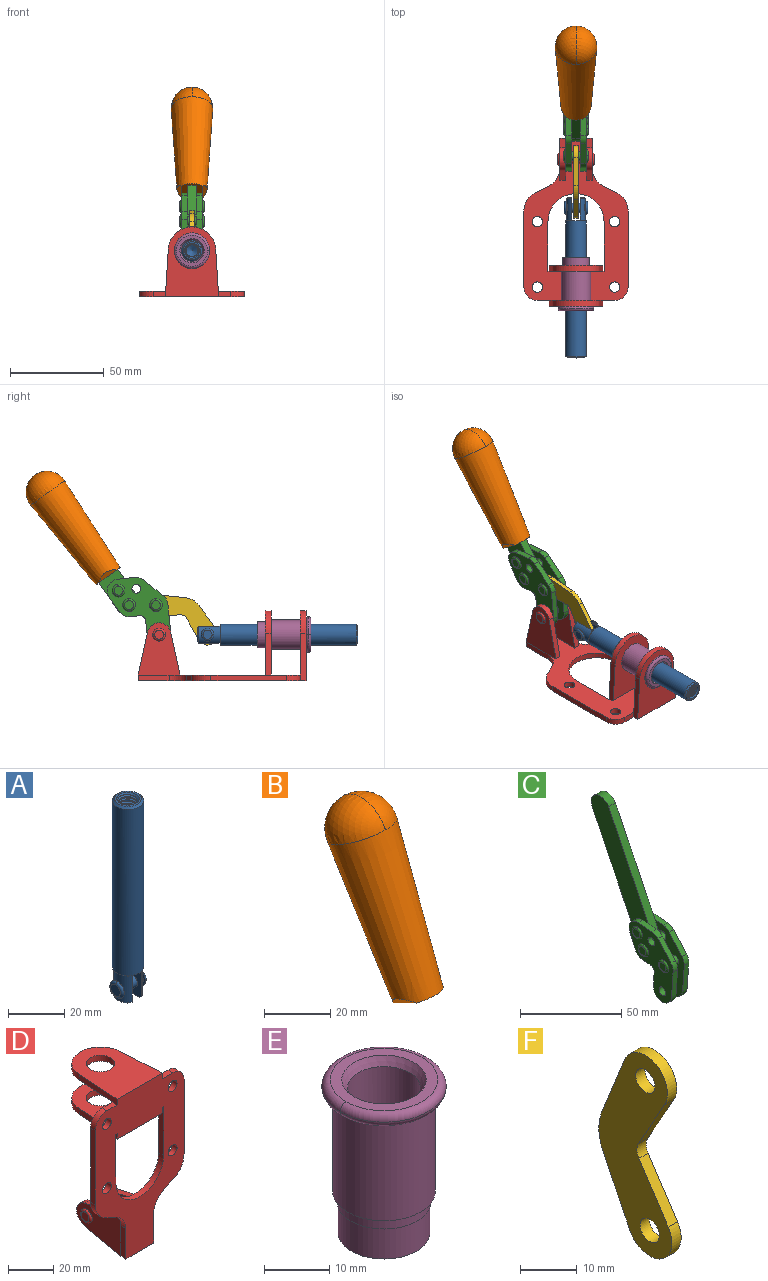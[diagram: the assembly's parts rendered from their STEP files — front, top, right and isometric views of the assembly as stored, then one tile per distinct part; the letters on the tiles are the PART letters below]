
ASSEMBLY  parts=6 mates=6
PART A: 48 faces, bbox 12.6x11.1x86.1 mm
  f0: torus R=2.41mm, axis (-1,0,0), area 15mm2, adj f30,f32,f34
  f1: torus R=2.41mm, axis (-1,0,0), area 15mm2, adj f29,f31,f33
  f2: cylinder r=5.54mm len=72.39mm, axis (0,0,1), area 2518.5mm2, adj f3,f4,f42,f43
  f3: cone r=5.54mm half-angle=45deg, axis (0,0,1), area 7.6mm2, adj f2,f5,f41
  f4: cone r=5.54mm half-angle=45deg, axis (0,0,-1), area 34.9mm2, adj f2,f39
  f5: cylinder r=5.08mm len=11.48mm, axis (0,0,1), area 108.3mm2, adj f3,f7,f8,f41
  f6: cylinder r=2.41mm len=4.83mm, axis (-1,0,0), area 71.2mm2, adj f40,f41
  f7: cylinder r=2.41mm len=4.83mm, axis (-1,0,0), area 7.6mm2, adj f5,f34
  f8: cone r=5.08mm half-angle=45deg, axis (0,0,1), area 10.6mm2, adj f5,f37,f41
  f9: cone r=3.98mm half-angle=45deg, axis (0,0,1), area 17.6mm2, adj f27,f39,f45,f46,f47
  f10: cylinder r=2.41mm len=4.83mm, axis (-1,0,0), area 7.6mm2, adj f33,f38
  f11: cylinder r=3.2mm len=6.4mm, axis (0,0,1), area 78.4mm2, adj f12,f28,f44,f45,f47
  f12: cylinder r=3.2mm len=6.4mm, axis (0,0,1), area 10.5mm2, adj f11,f13,f45,f47
  f13: cylinder r=3.2mm len=6.4mm, axis (0,0,1), area 10.5mm2, adj f12,f14,f45,f47
  f14: cylinder r=3.2mm len=6.4mm, axis (0,0,1), area 10.5mm2, adj f13,f15,f45,f47
  f15: cylinder r=3.2mm len=6.4mm, axis (0,0,1), area 10.5mm2, adj f14,f16,f45,f47
  f16: cylinder r=3.2mm len=6.4mm, axis (0,0,1), area 10.5mm2, adj f15,f17,f45,f47
  f17: cylinder r=3.2mm len=6.4mm, axis (0,0,1), area 10.5mm2, adj f16,f18,f45,f47
  f18: cylinder r=3.2mm len=6.4mm, axis (0,0,1), area 10.5mm2, adj f17,f19,f45,f47
  f19: cylinder r=3.2mm len=6.4mm, axis (0,0,1), area 10.5mm2, adj f18,f20,f45,f47
  f20: cylinder r=3.2mm len=6.4mm, axis (0,0,1), area 10.5mm2, adj f19,f21,f45,f47
  f21: cylinder r=3.2mm len=6.4mm, axis (0,0,1), area 10.5mm2, adj f20,f22,f45,f47
  f22: cylinder r=3.2mm len=6.4mm, axis (0,0,1), area 10.5mm2, adj f21,f23,f45,f47
  f23: cylinder r=3.2mm len=6.4mm, axis (0,0,1), area 10.5mm2, adj f22,f24,f45,f47
  f24: cylinder r=3.2mm len=6.4mm, axis (0,0,1), area 10.5mm2, adj f23,f25,f45,f47
  f25: cylinder r=3.2mm len=6.4mm, axis (0,0,1), area 10.5mm2, adj f24,f26,f45,f47
  f26: cylinder r=3.2mm len=6.4mm, axis (0,0,1), area 10.5mm2, adj f25,f27,f45,f47
  f27: cylinder r=3.2mm len=6.4mm, axis (0,0,1), area 7.4mm2, adj f9,f26,f45,f47
  f28: cone r=3.2mm half-angle=60deg, axis (0,0,1), area 37.2mm2, adj f11
  f29: plane 4.83x4.83mm, normal (-1,0,0), area 18.3mm2, adj f1,f31
  f30: plane 4.83x4.83mm, normal (1,0,0), area 18.3mm2, adj f0,f32
  f31: torus R=2.41mm, axis (-1,0,0), area 15mm2, adj f1,f29,f33
  f32: torus R=2.41mm, axis (-1,0,0), area 15mm2, adj f0,f30,f34
  f33: plane 6.83x6.83mm, normal (1,0,0), area 18.3mm2, adj f1,f10,f31
  f34: plane 6.83x6.83mm, normal (-1,0,0), area 18.3mm2, adj f0,f7,f32
  f35: cone r=5.08mm half-angle=45deg, axis (0,0,1), area 10.6mm2, adj f36,f38,f40
  f36: plane 7.25x1.97mm, normal (0,0,-1), area 10mm2, adj f35,f40
  f37: plane 7.25x1.97mm, normal (0,0,-1), area 10mm2, adj f8,f41
  f38: cylinder r=5.08mm len=11.48mm, axis (0,0,1), area 108.3mm2, adj f10,f35,f40,f42
  f39: plane 9.55x9.55mm, normal (0,0,1), area 22mm2, adj f4,f9
  f40: plane 12.76x10.09mm, normal (1,0,0), area 95.7mm2, adj f6,f35,f36,f38,f42,f43
  f41: plane 12.76x10.09mm, normal (-1,0,0), area 95.7mm2, adj f3,f5,f6,f8,f37,f43
  f42: cone r=5.54mm half-angle=45deg, axis (0,0,1), area 7.6mm2, adj f2,f38,f40
  f43: plane 11.07x4.7mm, normal (0,0,-1), area 50.4mm2, adj f2,f40,f41
  f44: plane 0.89x0.62mm, normal (-1,0,0), area 0.3mm2, adj f11,f45,f46,f47
  f45: bspline ~24.8x7.63mm, area 266.6mm2, adj f9,f11,f12,f13,f14,f15,f16,f17
  f46: bspline ~24.87x7.63mm, area 73.6mm2, adj f9,f44,f45,f47
  f47: bspline ~24.98x7.63mm, area 272.5mm2, adj f9,f11,f12,f13,f14,f15,f16,f17
PART B: 11 faces, bbox 22.3x42.6x64.5 mm
  f0: sphere r=11.13mm, area 411.4mm2, adj f1,f8
  f1: cone r=11.11mm half-angle=3.3deg, axis (0,0.44,0.9), area 3251.8mm2, adj f0,f7,f8,f9,f10
  f2: cylinder r=6.16mm len=11.7mm, axis (1,0,0), area 89.5mm2, adj f3,f4,f5,f6
  f3: plane 60.23x36.75mm, normal (-1,0,0), area 763.6mm2, adj f2,f4,f6,f10
  f4: plane 51.37x25.05mm, normal (0,0.9,-0.44), area 264.2mm2, adj f2,f3,f5,f10
  f5: plane 60.23x36.75mm, normal (1,0,0), area 763.6mm2, adj f2,f4,f6,f10
  f6: plane 51.37x25.05mm, normal (0,-0.9,0.44), area 264.2mm2, adj f2,f3,f5,f10
  f7: plane 9.95x5.95mm, normal (0.71,-0.31,-0.64), area 25.8mm2, adj f1,f10
  f8: sphere r=11.13mm, area 411.4mm2, adj f0,f1
  f9: plane 9.95x5.95mm, normal (-0.71,-0.31,-0.64), area 25.8mm2, adj f1,f10
  f10: plane 14.27x11.38mm, normal (0,-0.44,-0.9), area 106.7mm2, adj f1,f3,f4,f5,f6,f7,f9
PART C: 59 faces, bbox 12.9x60.2x99.6 mm
  f0: torus R=2.39mm, axis (-1,0,0), area 14.9mm2, adj f20,f43,f51
  f1: torus R=2.39mm, axis (-1,0,0), area 14.9mm2, adj f19,f42,f51
  f2: torus R=2.39mm, axis (-1,0,0), area 14.9mm2, adj f18,f35,f51
  f3: torus R=2.39mm, axis (-1,0,0), area 14.9mm2, adj f14,f17,f23
  f4: torus R=2.39mm, axis (-1,0,0), area 14.9mm2, adj f13,f16,f23
  f5: torus R=2.39mm, axis (-1,0,0), area 14.9mm2, adj f12,f15,f23
  f6: cylinder r=2.39mm len=4.78mm, axis (1,0,0), area 46.5mm2, adj f48,f50,f51
  f7: cylinder r=2.39mm len=4.78mm, axis (1,0,0), area 46.5mm2, adj f50,f51
  f8: cylinder r=6.35mm len=12.68mm, axis (1,0,0), area 61.8mm2, adj f38,f39,f50,f51
  f9: cylinder r=2.39mm len=4.78mm, axis (-1,0,0), area 70.5mm2, adj f46,f50
  f10: cylinder r=2.39mm len=4.78mm, axis (-1,0,0), area 46.5mm2, adj f23,f45,f46
  f11: cylinder r=2.39mm len=4.78mm, axis (-1,0,0), area 46.5mm2, adj f23,f46
  f12: plane 4.78x4.78mm, normal (1,0,0), area 17.9mm2, adj f5,f15
  f13: plane 4.78x4.78mm, normal (1,0,0), area 17.9mm2, adj f4,f16
  f14: plane 4.78x4.78mm, normal (1,0,0), area 17.9mm2, adj f3,f17
  f15: torus R=2.39mm, axis (-1,0,0), area 14.9mm2, adj f5,f12,f23
  f16: torus R=2.39mm, axis (-1,0,0), area 14.9mm2, adj f4,f13,f23
  f17: torus R=2.39mm, axis (-1,0,0), area 14.9mm2, adj f3,f14,f23
  f18: plane 4.78x4.78mm, normal (-1,0,0), area 17.9mm2, adj f2,f35
  f19: plane 4.78x4.78mm, normal (-1,0,0), area 17.9mm2, adj f1,f42
  f20: plane 4.78x4.78mm, normal (-1,0,0), area 17.9mm2, adj f0,f43
  f21: plane 2.26x0.2mm, normal (1,0,0), area 0.2mm2, adj f31,f44
  f22: plane 2.26x0.2mm, normal (-1,0,0), area 0.2mm2, adj f41,f44
  f23: plane 39.37x30.77mm, normal (1,0,0), area 565.5mm2, adj f3,f4,f5,f10,f11,f15,f16,f17
  f24: cylinder r=6.1mm len=4.15mm, axis (-1,0,0), area 14.7mm2, adj f23,f25,f32,f46
  f25: plane 10.25x9.01mm, normal (0,-0.75,0.66), area 42.3mm2, adj f23,f24,f26,f46
  f26: cylinder r=6.35mm len=4.64mm, axis (-1,0,0), area 15.6mm2, adj f23,f25,f27,f46
  f27: plane 15.84x3.1mm, normal (0,-1,-0.07), area 49.2mm2, adj f23,f26,f28,f46
  f28: cylinder r=6.35mm len=12.68mm, axis (-1,0,0), area 61.8mm2, adj f23,f27,f29,f46
  f29: plane 8.11x3.1mm, normal (0,1,0.07), area 25.2mm2, adj f23,f28,f30,f46
  f30: cylinder r=3.05mm len=3.25mm, axis (-1,0,0), area 14.8mm2, adj f23,f29,f31,f46
  f31: plane 5.99x3.1mm, normal (0,0.07,-1), area 18.6mm2, adj f21,f23,f30,f44,f46
  f32: plane 9.5x3.1mm, normal (0,-0.07,1), area 29.5mm2, adj f23,f24,f33,f46,f47
  f33: cylinder r=6.1mm len=8.63mm, axis (-1,0,0), area 39.1mm2, adj f23,f32,f34,f47
  f34: plane 8.65x3.96mm, normal (0,0.91,-0.42), area 29.5mm2, adj f23,f33,f44,f47
  f35: torus R=2.39mm, axis (-1,0,0), area 14.9mm2, adj f2,f18,f51
  f36: plane 10.25x9.01mm, normal (0,-0.75,0.66), area 42.3mm2, adj f37,f49,f50,f51
  f37: cylinder r=6.35mm len=4.64mm, axis (1,0,0), area 15.6mm2, adj f36,f38,f50,f51
  f38: plane 15.84x3.1mm, normal (0,-1,-0.07), area 49.2mm2, adj f8,f37,f50,f51
  f39: plane 8.11x3.1mm, normal (0,1,0.07), area 25.2mm2, adj f8,f40,f50,f51
  f40: cylinder r=3.05mm len=3.25mm, axis (1,0,0), area 14.8mm2, adj f39,f41,f50,f51
  f41: plane 5.99x3.1mm, normal (0,0.07,-1), area 18.6mm2, adj f22,f40,f44,f50,f51
  f42: torus R=2.39mm, axis (-1,0,0), area 14.9mm2, adj f1,f19,f51
  f43: torus R=2.39mm, axis (-1,0,0), area 14.9mm2, adj f0,f20,f51
  f44: cylinder r=6.35mm len=12.12mm, axis (-1,0,0), area 128.9mm2, adj f21,f22,f23,f31,f34,f41,f46,f47
  f45: plane 2.65x1.35mm, normal (1,0,0), area 1mm2, adj f10,f55
  f46: plane 39.08x20.42mm, normal (-1,0,0), area 412.5mm2, adj f9,f10,f11,f24,f25,f26,f27,f28
  f47: plane 77.62x39.82mm, normal (1,0,0), area 850mm2, adj f32,f33,f34,f44,f53,f54,f55
  f48: plane 2.65x1.35mm, normal (-1,0,0), area 1mm2, adj f6,f55
  f49: cylinder r=6.1mm len=4.15mm, axis (1,0,0), area 14.7mm2, adj f36,f50,f51,f56
  f50: plane 39.08x20.42mm, normal (1,0,0), area 412.5mm2, adj f6,f7,f8,f9,f36,f37,f38,f39
  f51: plane 39.37x30.77mm, normal (-1,0,0), area 565.5mm2, adj f0,f1,f2,f6,f7,f8,f35,f36
  f52: plane 8.65x3.96mm, normal (0,0.91,-0.42), area 29.5mm2, adj f44,f51,f57,f58
  f53: plane 68.49x33.4mm, normal (0,0.9,-0.44), area 358.1mm2, adj f44,f47,f54,f58
  f54: cylinder r=6.35mm len=12.06mm, axis (1,0,0), area 93.7mm2, adj f47,f53,f55,f58
  f55: plane 68.49x33.4mm, normal (0,-0.9,0.44), area 358.1mm2, adj f44,f45,f46,f47,f48,f50,f54,f58
  f56: plane 9.5x3.1mm, normal (0,-0.07,1), area 29.5mm2, adj f49,f50,f51,f57,f58
  f57: cylinder r=6.1mm len=8.63mm, axis (1,0,0), area 39.1mm2, adj f51,f52,f56,f58
  f58: plane 77.62x39.82mm, normal (-1,0,0), area 850mm2, adj f44,f52,f53,f54,f55,f56,f57
PART D: 55 faces, bbox 55.7x37.4x89.8 mm
  f0: torus R=2.41mm, axis (-1,0,0), area 15mm2, adj f11,f15,f25
  f1: torus R=2.41mm, axis (-1,0,0), area 15mm2, adj f10,f12,f22
  f2: cylinder r=2.78mm len=5.56mm, axis (0,-1,0), area 54.2mm2, adj f30,f54
  f3: cylinder r=14.99mm len=29.97mm, axis (0,-1,0), area 145.9mm2, adj f30,f49,f53,f54
  f4: cylinder r=2.78mm len=5.56mm, axis (0,-1,0), area 54.2mm2, adj f30,f54
  f5: cylinder r=2.78mm len=5.56mm, axis (0,-1,0), area 54.2mm2, adj f30,f54
  f6: cylinder r=2.78mm len=5.56mm, axis (0,-1,0), area 54.2mm2, adj f30,f54
  f7: cylinder r=6.35mm len=12.7mm, axis (0,0,1), area 123.6mm2, adj f27,f51
  f8: cylinder r=6.35mm len=12.7mm, axis (0,0,-1), area 124.7mm2, adj f21,f35
  f9: cylinder r=2.41mm len=11.18mm, axis (-1,0,0), area 169.4mm2, adj f16,f19
  f10: plane 4.83x4.83mm, normal (1,0,0), area 18.3mm2, adj f1,f12
  f11: plane 4.83x4.83mm, normal (-1,0,0), area 18.3mm2, adj f0,f15
  f12: torus R=2.41mm, axis (-1,0,0), area 15mm2, adj f1,f10,f22
  f13: cylinder r=6.35mm len=12.41mm, axis (1,0,0), area 53.4mm2, adj f18,f19,f22,f23
  f14: cylinder r=6.35mm len=12.41mm, axis (-1,0,0), area 53.4mm2, adj f16,f17,f24,f25
  f15: torus R=2.41mm, axis (-1,0,0), area 15mm2, adj f0,f11,f25
  f16: plane 27.86x22.35mm, normal (1,0,0), area 425.4mm2, adj f9,f14,f17,f24,f30
  f17: plane 22.86x4.97mm, normal (0,0.21,0.98), area 72.5mm2, adj f14,f16,f25,f30
  f18: plane 22.86x4.97mm, normal (0,0.21,0.98), area 72.5mm2, adj f13,f19,f22,f30
  f19: plane 27.86x22.35mm, normal (-1,0,0), area 425.4mm2, adj f9,f13,f18,f23,f30
  f20: cylinder r=12.7mm len=25.35mm, axis (0,0,-1), area 119.8mm2, adj f21,f34,f35,f36
  f21: plane 34.21x28.07mm, normal (0,0,-1), area 702.4mm2, adj f8,f20,f30,f34,f36
  f22: plane 27.96x22.45mm, normal (1,0,0), area 407.2mm2, adj f1,f12,f13,f18,f23,f30,f42,f43
  f23: plane 22.86x4.97mm, normal (0,0.21,-0.98), area 72.5mm2, adj f13,f19,f22,f44
  f24: plane 22.86x4.97mm, normal (0,0.21,-0.98), area 72.5mm2, adj f14,f16,f25,f44
  f25: plane 27.86x22.35mm, normal (-1,0,0), area 407.1mm2, adj f0,f14,f15,f17,f24,f30,f45,f46
  f26: plane 3.1x0.95mm, normal (0,0,-1), area 2.7mm2, adj f30,f49,f50,f54
  f27: plane 34.21x28.07mm, normal (0,0,1), area 702.4mm2, adj f7,f28,f30,f50,f52
  f28: cylinder r=12.7mm len=25.35mm, axis (0,0,1), area 118.8mm2, adj f27,f50,f51,f52
  f29: plane 3.1x0.95mm, normal (0,0,-1), area 2.7mm2, adj f30,f52,f53,f54
  f30: plane 86.54x55.63mm, normal (0,1,0), area 2362.9mm2, adj f2,f3,f4,f5,f6,f16,f17,f18
  f31: plane 40.56x3.1mm, normal (-1,0,0), area 125.7mm2, adj f30,f32,f48,f54
  f32: cylinder r=7.11mm len=7.11mm, axis (0,-1,0), area 34.6mm2, adj f30,f31,f33,f54
  f33: plane 6.67x3.1mm, normal (0,0,1), area 20.4mm2, adj f30,f32,f34,f54
  f34: plane 25.39x3.13mm, normal (-1,0.06,0), area 79.5mm2, adj f20,f21,f33,f35,f54
  f35: plane 37.31x28.45mm, normal (0,0,1), area 789.9mm2, adj f8,f20,f34,f36,f54
  f36: plane 25.39x3.13mm, normal (1,0.06,0), area 79.5mm2, adj f20,f21,f35,f37,f54
  f37: plane 6.67x3.1mm, normal (0,0,1), area 20.4mm2, adj f30,f36,f38,f54
  f38: cylinder r=7.11mm len=7.11mm, axis (0,-1,0), area 34.6mm2, adj f30,f37,f39,f54
  f39: plane 40.56x3.1mm, normal (1,0,0), area 125.7mm2, adj f30,f38,f40,f54
  f40: cylinder r=11.18mm len=10.16mm, axis (0,-1,0), area 39.5mm2, adj f30,f39,f41,f54
  f41: plane 6.09x3.1mm, normal (0.42,0,-0.91), area 20.8mm2, adj f30,f40,f42,f54
  f42: cylinder r=11.18mm len=9.41mm, axis (0,-1,0), area 37.2mm2, adj f22,f30,f41,f43,f54
  f43: plane 16.5x3.1mm, normal (1,0,0), area 51.1mm2, adj f22,f42,f44,f54
  f44: plane 17.37x3.1mm, normal (0,0,-1), area 53.8mm2, adj f23,f24,f30,f43,f45,f54
  f45: plane 16.5x3.1mm, normal (-1,0,0), area 51.1mm2, adj f25,f44,f46,f54
  f46: cylinder r=11.18mm len=9.41mm, axis (0,-1,0), area 37.2mm2, adj f25,f30,f45,f47,f54
  f47: plane 6.09x3.1mm, normal (-0.42,0,-0.91), area 20.8mm2, adj f30,f46,f48,f54
  f48: cylinder r=11.18mm len=10.16mm, axis (0,-1,0), area 39.5mm2, adj f30,f31,f47,f54
  f49: plane 26.54x3.1mm, normal (-1,0,0), area 82.3mm2, adj f3,f26,f30,f54
  f50: plane 25.39x3.1mm, normal (1,0.06,0), area 78.8mm2, adj f26,f27,f28,f51,f54
  f51: plane 37.31x28.45mm, normal (0,0,-1), area 789.9mm2, adj f7,f28,f50,f52,f54
  f52: plane 25.39x3.1mm, normal (-1,0.06,0), area 78.8mm2, adj f27,f28,f29,f51,f54
  f53: plane 26.54x3.1mm, normal (1,0,0), area 82.3mm2, adj f3,f29,f30,f54
  f54: plane 89.66x55.63mm, normal (0,-1,0), area 2678.5mm2, adj f2,f3,f4,f5,f6,f26,f29,f31
PART E: 15 faces, bbox 20.6x20.6x28.7 mm
  f0: torus R=8.26mm, axis (0,0,1), area 56.8mm2, adj f1,f10,f12
  f1: torus R=8.26mm, axis (0,0,1), area 56.8mm2, adj f0,f6,f13
  f2: cylinder r=5.59mm len=25.91mm, axis (0,0,1), area 909.6mm2, adj f3,f4
  f3: cone r=6.86mm half-angle=45deg, axis (0,0,-1), area 70.2mm2, adj f2,f14
  f4: cone r=6.47mm half-angle=30deg, axis (0,0,1), area 66.7mm2, adj f2,f13
  f5: cylinder r=7.04mm len=14.07mm, axis (0,0,1), area 252.6mm2, adj f11,f14
  f6: torus R=8.26mm, axis (0,0,1), area 56.8mm2, adj f1,f12,f13
  f7: cylinder r=7.16mm len=14.33mm, axis (0,0,1), area 91.5mm2, adj f9,f11
  f8: cylinder r=7.86mm len=18.42mm, axis (0,0,1), area 909.6mm2, adj f9,f10
  f9: plane 15.72x15.72mm, normal (0,0,-1), area 33mm2, adj f7,f8
  f10: plane 16.51x16.51mm, normal (0,0,-1), area 19.9mm2, adj f0,f8,f12
  f11: plane 14.33x14.33mm, normal (0,0,-1), area 5.7mm2, adj f5,f7
  f12: torus R=8.26mm, axis (0,0,1), area 56.8mm2, adj f0,f6,f10
  f13: plane 16.51x16.51mm, normal (0,0,1), area 82.7mm2, adj f1,f4,f6
  f14: plane 14.07x14.07mm, normal (0,0,-1), area 7.8mm2, adj f3,f5
PART F: 12 faces, bbox 2.3x18.2x42.8 mm
  f0: cylinder r=2.4mm len=4.8mm, axis (1,0,0), area 34.9mm2, adj f4,f11
  f1: cylinder r=10.41mm len=8.47mm, axis (1,0,0), area 20.2mm2, adj f4,f9,f10,f11
  f2: cylinder r=3.05mm len=3.16mm, axis (1,0,0), area 7.7mm2, adj f4,f6,f7,f11
  f3: cylinder r=2.4mm len=4.8mm, axis (1,0,0), area 34.9mm2, adj f4,f11
  f4: plane 42.81x18.23mm, normal (-1,0,0), area 414.1mm2, adj f0,f1,f2,f3,f5,f6,f7,f8
  f5: cylinder r=5.54mm len=10.67mm, axis (1,0,0), area 41.8mm2, adj f4,f6,f10,f11
  f6: plane 11.66x6.53mm, normal (0,-0.87,-0.49), area 30.9mm2, adj f2,f4,f5,f11
  f7: plane 11.17x7.33mm, normal (0,-0.84,0.55), area 30.9mm2, adj f2,f4,f8,f11
  f8: cylinder r=5.54mm len=10.51mm, axis (1,0,0), area 41.8mm2, adj f4,f7,f9,f11
  f9: plane 13.67x6.67mm, normal (0,0.9,-0.44), area 35.1mm2, adj f1,f4,f8,f11
  f10: plane 14.1x5.7mm, normal (0,0.93,0.37), area 35.1mm2, adj f1,f4,f5,f11
  f11: plane 42.81x18.23mm, normal (1,0,0), area 414.1mm2, adj f0,f1,f2,f3,f5,f6,f7,f8
PLACE A rot(axis=(1,0,0),90deg) t=(0,31.11,0)mm
PLACE B rot(axis=(-1,0,0),10deg) t=(0,22.86,60.49)mm
PLACE C rot(axis=(-1,0,0),10deg) t=(0,22.86,60.49)mm
PLACE D rot(axis=(1,0,0),90deg) t=(0,9.43,0)mm fixed
PLACE E rot(axis=(1,0,0),90deg) t=(0,9.43,0)mm
PLACE F rot(axis=(1,0,0),121.8deg) t=(0,41.76,11.86)mm
MATE revolute F.f3 <-> C.f4  axis (1,0,0) through (0,43.18,40.4)mm
MATE revolute F.f5 <-> A.f6  axis (1,0,0) through (0,15.64,24.61)mm
MATE fastened C.f54 <-> B.f2  axis (1,0,0) through (0,102.33,102.1)mm
MATE revolute D.f0 <-> C.f7  axis (-1,0,0) through (0,41.52,24.61)mm
MATE slider D.f7 <-> A.f2  axis (0,-1,0) through (0,-36.96,24.61)mm
MATE fastened E.f0 <-> D.f7  axis (0,1,0) through (0,-36.96,24.61)mm
